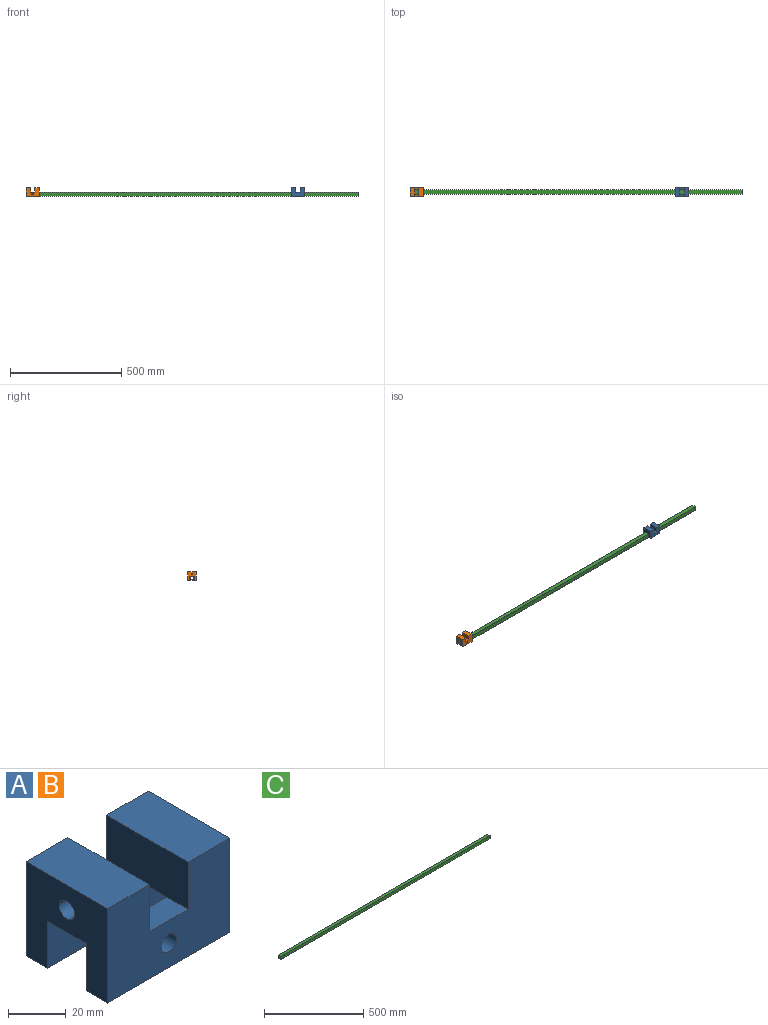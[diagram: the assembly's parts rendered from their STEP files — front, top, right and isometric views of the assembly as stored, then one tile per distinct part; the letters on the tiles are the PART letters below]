
ASSEMBLY  parts=3 mates=2
PART A: 18 faces, bbox 60x40x40 mm
  f0: plane 60x20mm, normal (0,-1,0), area 1200mm2, adj f1,f2,f3,f6,f10,f11
  f1: plane 40x40mm, normal (-1,0,0), area 1175.8mm2, adj f0,f2,f8,f9,f10,f12,f13,f15
  f2: plane 60x10.5mm, normal (0,0,-1), area 630mm2, adj f0,f1,f3,f9
  f3: plane 40x40mm, normal (1,0,0), area 1220mm2, adj f0,f2,f4,f9,f11,f12,f13,f15
  f4: plane 40x20.5mm, normal (0,0,1), area 820mm2, adj f3,f5,f9,f15
  f5: plane 40x20mm, normal (-1,0,0), area 800mm2, adj f4,f6,f9,f11,f14,f15
  f6: plane 19x10.5mm, normal (0,0,1), area 199.5mm2, adj f0,f5,f7,f9
  f7: plane 40x20mm, normal (1,0,0), area 755.8mm2, adj f6,f8,f9,f10,f14,f15,f17
  f8: plane 40x20.5mm, normal (0,0,1), area 820mm2, adj f1,f7,f9,f15
  f9: plane 60x40mm, normal (0,1,0), area 2020mm2, adj f1,f2,f3,f4,f5,f6,f7,f8
  f10: plane 20.5x19mm, normal (0,0,-1), area 389.5mm2, adj f0,f1,f7,f12
  f11: plane 20.5x19mm, normal (0,0,-1), area 389.5mm2, adj f0,f3,f5,f12
  f12: plane 60x20mm, normal (0,1,0), area 1155.8mm2, adj f1,f3,f10,f11,f13,f14,f16
  f13: plane 60x10.5mm, normal (0,0,-1), area 630mm2, adj f1,f3,f12,f15
  f14: plane 19x10.5mm, normal (0,0,1), area 199.5mm2, adj f5,f7,f12,f15
  f15: plane 60x40mm, normal (0,-1,0), area 1975.8mm2, adj f1,f3,f4,f5,f7,f8,f13,f14
  f16: cylinder r=3.75mm len=10.5mm, axis (0,-1,0), area 247.4mm2, adj f12,f15
  f17: cylinder r=3.75mm len=20.5mm, axis (-1,0,0), area 483mm2, adj f1,f7
PART B: same geometry as A
PART C: 10 faces, bbox 1490x19x19 mm
  f0: plane 1490x19mm, normal (0,-1,0), area 28310mm2, adj f1,f3,f4,f5
  f1: plane 1490x19mm, normal (0,0,-1), area 28310mm2, adj f0,f2,f4,f5
  f2: plane 1490x19mm, normal (0,1,0), area 28310mm2, adj f1,f3,f4,f5
  f3: plane 1490x19mm, normal (0,0,1), area 28310mm2, adj f0,f2,f4,f5
  f4: plane 19x19mm, normal (1,0,0), area 105mm2, adj f0,f1,f2,f3,f6,f7,f8,f9
  f5: plane 19x19mm, normal (-1,0,0), area 105mm2, adj f0,f1,f2,f3,f6,f7,f8,f9
  f6: plane 1490x16mm, normal (0,1,0), area 23840mm2, adj f4,f5,f7,f9
  f7: plane 1490x16mm, normal (0,0,1), area 23840mm2, adj f4,f5,f6,f8
  f8: plane 1490x16mm, normal (0,-1,0), area 23840mm2, adj f4,f5,f7,f9
  f9: plane 1490x16mm, normal (0,0,-1), area 23840mm2, adj f4,f5,f6,f8
PLACE A rot(axis=(0,0,-1),180deg) t=(1240.41,29.23,39.26)mm
PLACE B t=(-10.25,-10.77,39.26)mm
PLACE C t=(-10.25,-0.27,0.26)mm
MATE slider C.f4 <-> A.f1  axis (1,0,0) through (1479.75,9.23,19.26)mm
MATE slider C.f5 <-> B.f1  axis (-1,0,0) through (-10.25,9.23,19.26)mm
